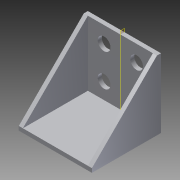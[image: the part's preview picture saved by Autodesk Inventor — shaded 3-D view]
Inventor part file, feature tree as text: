
AUTODESK INVENTOR PART (.ipt)
format: ipt  version: 2014 (Build 180170000, 170)  size: 118,272 bytes
history: native  units: in
note: dims shown in document units (in); Inventor stores cm internally (conversion verified against a paired STEP export)
features: extrude x3, sketch x3, plane x1, mirror x1
ambient origin geometry x8: Origin, YZ Plane, XZ Plane, XY Plane, X Axis, Y Axis, Z Axis, Center Point
bodies: Solid1 (feature_tree)
feature tree (8):
  extrude  "Extrusion1"  Depth=1.0in
  extrude  "Extrusion2"  Depth=0.25in
  plane  "Work Plane1"
  mirror  "Mirror1"
  extrude  "Extrusion3"  Depth=0.0625in TaperAngle=0.0deg
  sketch  "Sketch1"  dims[d0=1.0in d1=1.0in]
  sketch  "Sketch2"  dims[d2=0.196in d3=0.25in]
  sketch  "Sketch3"  dims[d4=0.25in d5=0.0625in d6=0.0in d7=45.0deg d8=0.0625in d9=0.0in d10=-0.5in d11=0.0625in d12=0.0in]
